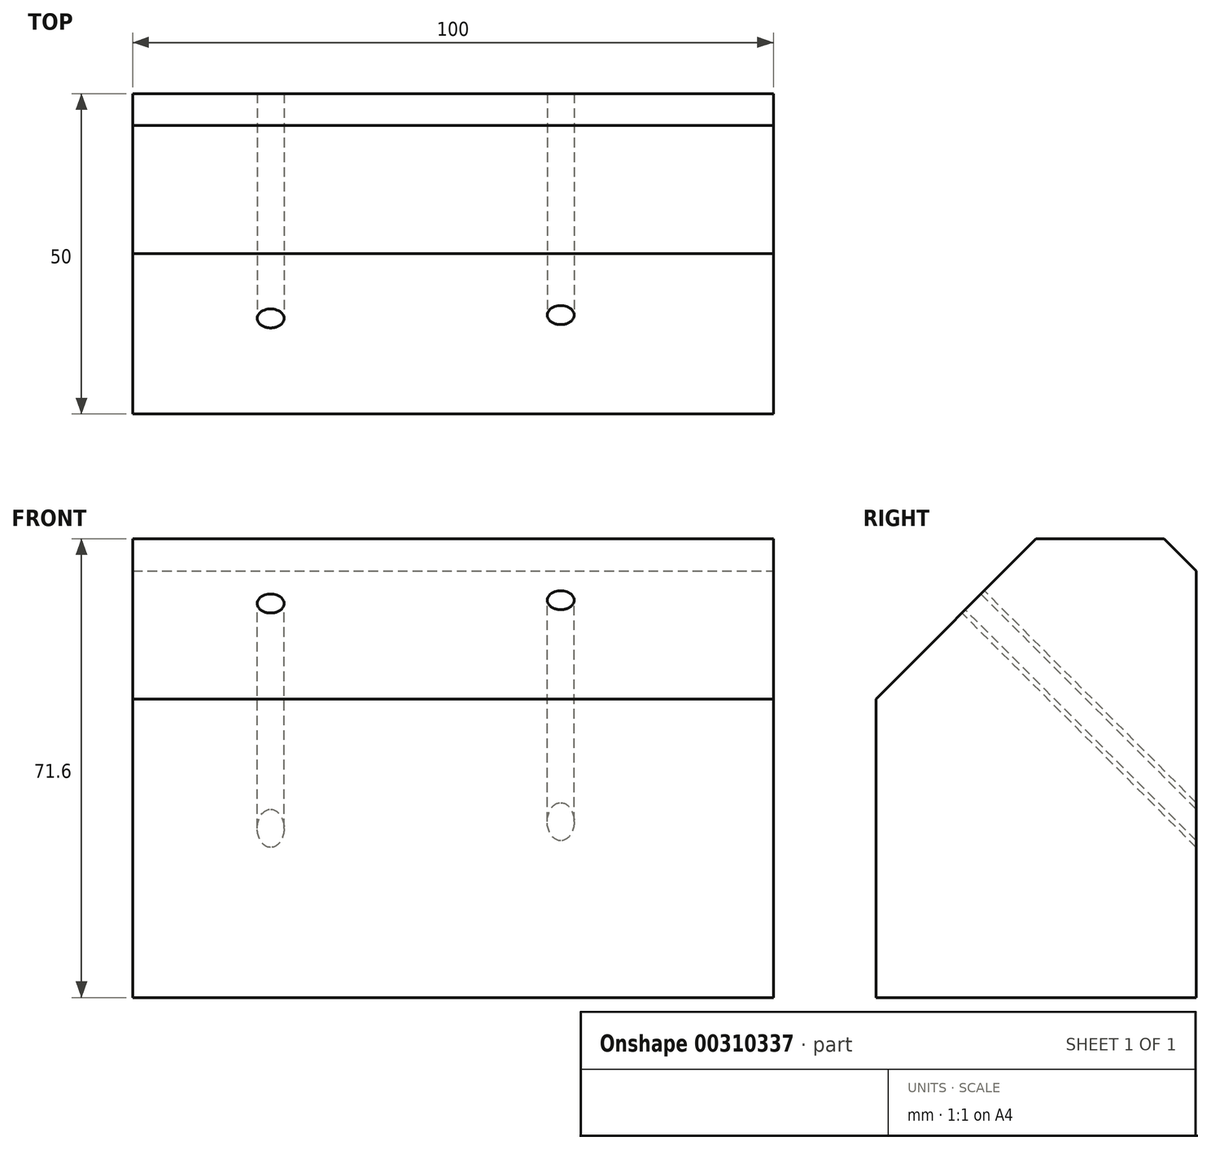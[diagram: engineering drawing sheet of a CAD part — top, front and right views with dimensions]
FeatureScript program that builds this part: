
annotation { "Feature Type Name" : "Feature", "Feature Type Description" : "" }
export const myFeature = defineFeature(function(context is Context, id is Id, definition is map)
    precondition{}
    {
        {
            var Q0;
            Q0=qCreatedBy(makeId("Top.planeOp"),FACE);
            var sketch = newSketch(context, id + "F0", { "sketchPlane" : qUnion([Q0])});
            skLineSegment(sketch, "E0.bottom", {"start": v(0, 0) * mm, "end": v(100, 0) * mm});
            skLineSegment(sketch, "E0.top", {"start": v(0, 50) * mm, "end": v(100, 50) * mm});
            skLineSegment(sketch, "E0.left", {"start": v(0, 0) * mm, "end": v(0, 50) * mm});
            skLineSegment(sketch, "E0.right", {"start": v(100, 0) * mm, "end": v(100, 50) * mm});
            skSolve(sketch);
        }
        {
            var Q0;
            Q0=makeQuery(id+"F0.imprint","IMPRINT",FACE,{"disambiguationData":[TD([[makeQuery(id+"F0.imprint","IMPRINT",EDGE,{"derivedFrom":sQuery(id+"F0.wireOp",EDGE,"E0.bottom")}),1.0]])]});
            extrude(context, id + "F1", {"entities" : qUnion([Q0]), "depth" : 71.6 * mm});
        }
        {
            var Q0;
            Q0=makeQuery(id+"F1.opExtrude","CAP_EDGE",EDGE,{"disambiguationData":[OSD([sQuery(id+"F0.wireOp",EDGE,"E0.bottom")])],"isStart":false});
            chamfer(context, id + "F2", {"entities" : qUnion([Q0]), "width" : 25 * mm, "tangentPropagation" : true});
        }
        {
            var Q0;
            Q0=makeQuery(id+"F2.opChamfer","BLEND_FACE",FACE,{"disambiguationData":[OSD([sQuery(id+"F0.wireOp",EDGE,"E0.bottom")])]});
            var sketch = newSketch(context, id + "F3", { "sketchPlane" : qUnion([Q0])});
            skPoint(sketch, "E1", {"position": v(21.53, 54.03) * mm});
            skPoint(sketch, "E2", {"position": v(66.8, 54.76) * mm});
            skSolve(sketch);
        }
        {
            var Q0;
            Q0=sQuery(id+"F3.wireOp",VERTEX,"E2");
            var Q1;
            Q1=sQuery(id+"F3.wireOp",VERTEX,"E1");
            var Q2;
            Q2=makeQuery(id+"F1.opExtrude","SWEPT_BODY",BODY,{"disambiguationData":[OSD([sQuery(id+"F0.wireOp",EDGE,"E0.bottom"),sQuery(id+"F0.wireOp",EDGE,"E0.top"),sQuery(id+"F0.wireOp",EDGE,"E0.left"),sQuery(id+"F0.wireOp",EDGE,"E0.right")])]});
            hole(context, id + "F4", {"style" : HoleStyle.SIMPLE, "endStyle" : HoleEndStyle.THROUGH, "standardTappedOrClearance" : lookupTablePath({ "standard" : "ISO", "engagement" : "75%", "pitch" : "0.8 mm", "size" : "M5", "type" : "Tapped" }), "standardBlindInLast" : lookupTablePath({ "standard" : "ISO", "engagement" : "75%", "pitch" : "0.8 mm", "size" : "M5", "type" : "Tapped" }), "holeDiameter" : 4.2 * mm, "showTappedDepth" : true, "tappedDepth" : 12 * mm, "tapClearance" : 3, "locations" : qUnion([Q0, Q1]), "scope" : qUnion([Q2]), "majorDiameter" : 5 * mm});
        }
        {
            var Q0;
            Q0=makeQuery(id+"F1.opExtrude","CAP_EDGE",EDGE,{"disambiguationData":[OSD([sQuery(id+"F0.wireOp",EDGE,"E0.top")])],"isStart":false});
            chamfer(context, id + "F5", {"entities" : qUnion([Q0]), "width" : 5 * mm, "tangentPropagation" : true});
        }
    });
